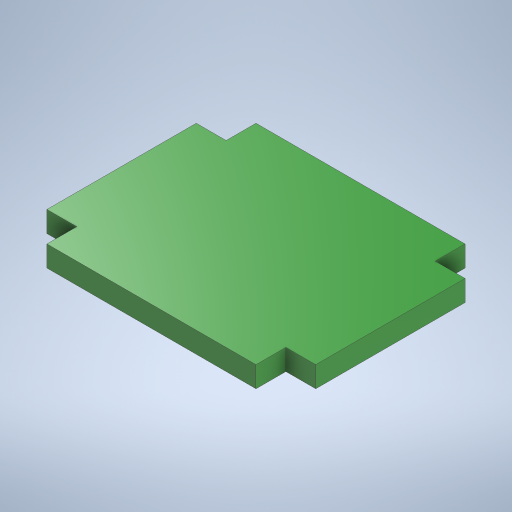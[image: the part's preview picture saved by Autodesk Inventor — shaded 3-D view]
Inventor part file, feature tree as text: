
AUTODESK INVENTOR PART (.ipt)
format: ipt  version: 2024.1 (Build 281209000, 209)  size: 248,320 bytes
history: native  units: mm
features: extrude x1, sketch x1
ambient origin geometry x8: Origin, YZ Plane, XZ Plane, XY Plane, X Axis, Y Axis, Z Axis, Center Point
bodies: Solide1 (feature_tree)
feature tree (2):
  extrude  "Extrusion1"  Depth=2.0mm
  sketch  "Esquisse1"
